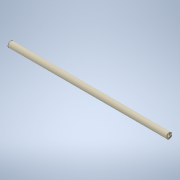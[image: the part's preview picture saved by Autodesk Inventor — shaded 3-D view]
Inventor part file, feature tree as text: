
AUTODESK INVENTOR PART (.ipt)
format: ipt  version: 2022 (Build 260153000, 153)  size: 128,512 bytes
history: native  units: mm
features: extrude x3, sketch x3, other x1, projected_geometry x1
ambient origin geometry x8: Origin, YZ Plane, XZ Plane, XY Plane, X Axis, Y Axis, Z Axis, Center Point
bodies: Solid (feature_tree)
feature tree (8):
  other  "Твердое тело1"
  extrude  "Выдавливание1"  Depth=610.0mm TaperAngle=0.0deg
  extrude  "Выдавливание2"  Depth=1.0mm TaperAngle=0.0deg
  extrude  "Выдавливание3"  Depth=3.0mm TaperAngle=0.0deg
  sketch  "Эскиз1"
  sketch  "Эскиз2"
  sketch  "Эскиз3"
  projected_geometry  "Спроецированная петля1"
